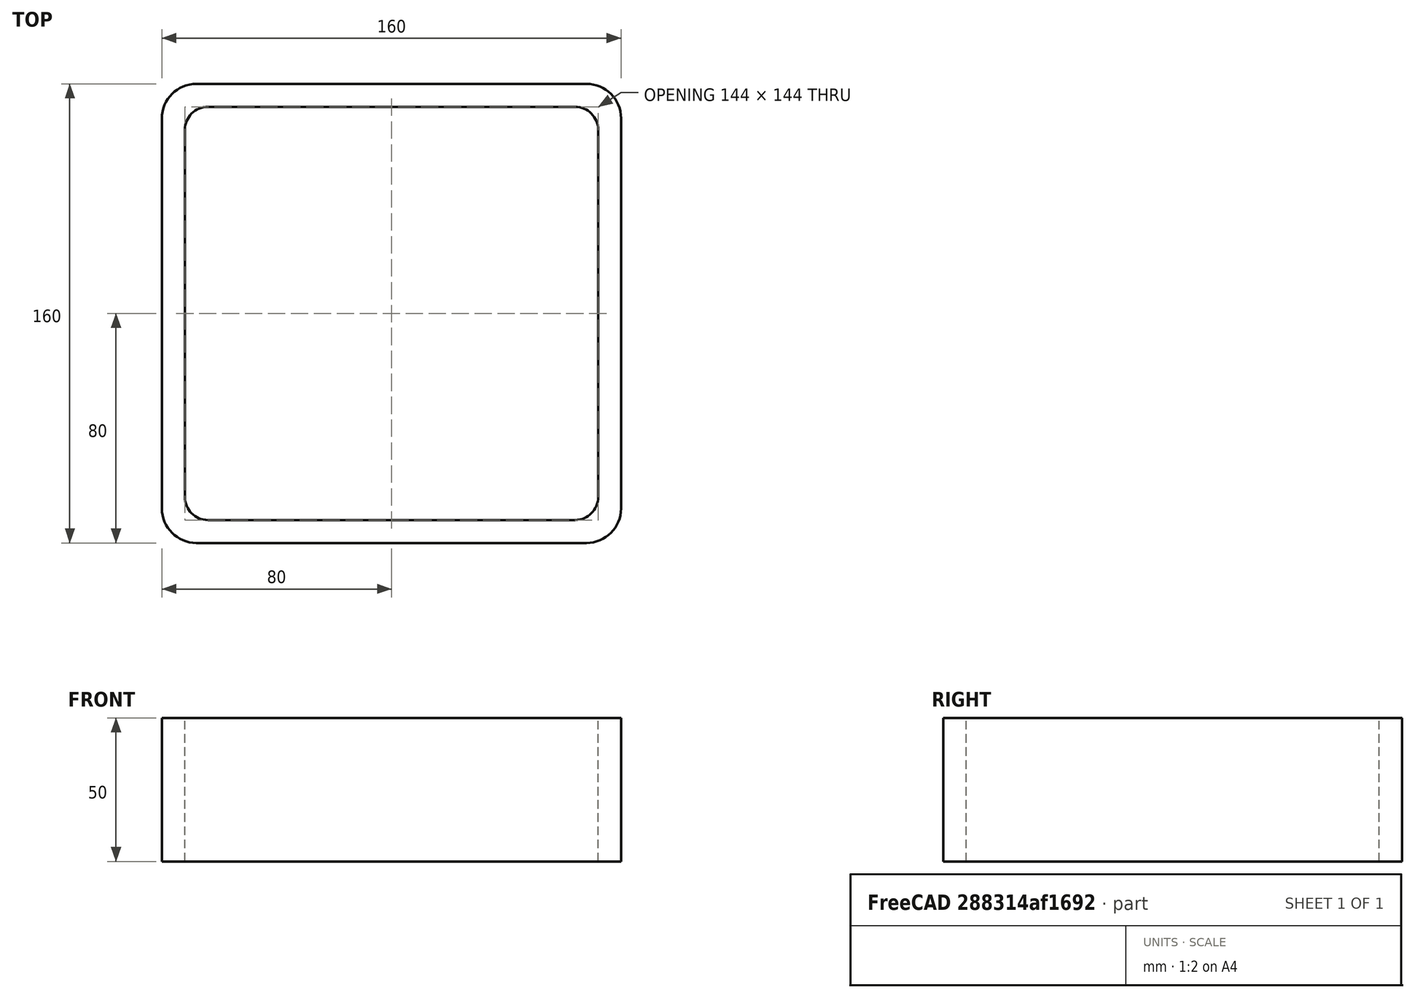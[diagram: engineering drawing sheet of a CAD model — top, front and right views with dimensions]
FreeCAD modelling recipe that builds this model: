
FCSTD DOCUMENT  (FreeCAD 0.15R4671 (Git))
Label: Square hollow section 160x160x8 EN10219 S235JRH
License: All rights reserved
LicenseURL: http://en.wikipedia.org/wiki/All_rights_reserved
objects: Sketcher::SketchObject×1, Part::Extrusion×1
note: 2 computed .brp shape members not serialized (recipe doc carries the construction recipe); baked Part::Feature solids carry a one-line shape summary decoded from their .brp

FEATURE [Sketcher::SketchObject] Sketch
  sketch-geometry (16):
    g0: LineSegment StartX=-64 StartY=72 StartZ=0 EndX=64 EndY=72 EndZ=0
    g1: LineSegment StartX=72 StartY=64 StartZ=0 EndX=72 EndY=-64 EndZ=0
    g2: LineSegment StartX=64 StartY=-72 StartZ=0 EndX=-64 EndY=-72 EndZ=0
    g3: LineSegment StartX=-72 StartY=-64 StartZ=0 EndX=-72 EndY=64 EndZ=0
    g4: LineSegment StartX=-68 StartY=80 StartZ=0 EndX=68 EndY=80 EndZ=0
    g5: LineSegment StartX=80 StartY=68 StartZ=0 EndX=80 EndY=-68 EndZ=0
    g6: LineSegment StartX=68 StartY=-80 StartZ=0 EndX=-68 EndY=-80 EndZ=0
    g7: LineSegment StartX=-80 StartY=-68 StartZ=0 EndX=-80 EndY=68 EndZ=0
    g8: ArcOfCircle CenterX=-64 CenterY=64 CenterZ=0 NormalX=0 NormalY=0 NormalZ=1 Radius=8 StartAngle=1.5708 EndAngle=3.14159
    g9: ArcOfCircle CenterX=64 CenterY=64 CenterZ=0 NormalX=0 NormalY=0 NormalZ=1 Radius=8 StartAngle=0 EndAngle=1.5708
    g10: ArcOfCircle CenterX=64 CenterY=-64 CenterZ=0 NormalX=0 NormalY=0 NormalZ=1 Radius=8 StartAngle=4.71239 EndAngle=6.28319
    g11: ArcOfCircle CenterX=-64 CenterY=-64 CenterZ=0 NormalX=0 NormalY=0 NormalZ=1 Radius=8 StartAngle=3.14159 EndAngle=4.71239
    g12: ArcOfCircle CenterX=68 CenterY=68 CenterZ=0 NormalX=0 NormalY=0 NormalZ=1 Radius=12 StartAngle=0 EndAngle=1.5708
    g13: ArcOfCircle CenterX=68 CenterY=-68 CenterZ=0 NormalX=0 NormalY=0 NormalZ=1 Radius=12 StartAngle=4.71239 EndAngle=6.28319
    g14: ArcOfCircle CenterX=-68 CenterY=-68 CenterZ=0 NormalX=0 NormalY=0 NormalZ=1 Radius=12 StartAngle=3.14159 EndAngle=4.71239
    g15: ArcOfCircle CenterX=-68 CenterY=68 CenterZ=0 NormalX=0 NormalY=0 NormalZ=1 Radius=12 StartAngle=1.5708 EndAngle=3.14159
  constraints (36):
    c: Horizontal(g2)
    c: Vertical(g3)
    c: Horizontal(g6)
    c: Vertical(g7)
    c: Tangent(g3,g8) = 1.5708
    c: Tangent(g0,g8) = 1.5708
    c: Tangent(g0,g9) = 1.5708
    c: Tangent(g1,g9) = 1.5708
    c: Tangent(g1,g10) = 1.5708
    c: Tangent(g2,g10) = 1.5708
    c: Tangent(g2,g11) = 1.5708
    c: Tangent(g3,g11) = 1.5708
    c: Tangent(g4,g12) = 1.5708
    c: Tangent(g5,g12) = 1.5708
    c: Tangent(g5,g13) = 1.5708
    c: Tangent(g6,g13) = 1.5708
    c: Tangent(g6,g14) = 1.5708
    c: Tangent(g7,g14) = 1.5708
    c: Tangent(g7,g15) = 1.5708
    c: Tangent(g4,g15) = 1.5708
    c: Equal(g9,g8)
    c: Equal(g9,g11)
    c: Equal(g9,g10)
    c: Equal(g12,g15)
    c: Equal(g12,g14)
    c: Equal(g12,g13)
    c: Symmetric(g4,g6,g-1)
    c: Symmetric(g7,g5,g-2)
    c: DistanceY(g4,g6) = -160
    c: DistanceX(g7,g5) = 160
    c: Symmetric(g3,g1,g-2)
    c: Symmetric(g0,g2,g-1)
    c: DistanceY(g0,g4) = 8
    c: DistanceX(g5,g1) = -8
    c: Radius(g9) = 8
    c: Radius(g12) = 12
FEATURE [Part::Extrusion] Extrude  label="Square hollow section 160x160x8 EN10219 S235JRH"
  Base = -> Sketch
  Dir = (0,0,50)
  Solid = true
